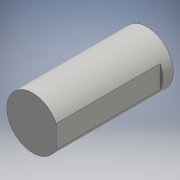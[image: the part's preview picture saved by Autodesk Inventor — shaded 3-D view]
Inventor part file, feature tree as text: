
AUTODESK INVENTOR PART (.ipt)
format: ipt  version: 2016 (Build 200138000, 138)  size: 95,744 bytes
history: native  units: mm
features: extrude x2, sketch x2, other x1
ambient origin geometry x8: Origin, YZ Plane, XZ Plane, XY Plane, X Axis, Y Axis, Z Axis, Center Point
bodies: Body1 (feature_tree)
feature tree (5):
  other  "ソリッド1"
  extrude  "押し出し1"  Depth=10.0mm
  extrude  "押し出し2"  Depth=22.0mm TaperAngle=0.0deg
  sketch  "スケッチ1"
  sketch  "スケッチ2"
